# Revit family: TD92_BPA386_AMA003_RVT20_R00
name_source: partatom
category: Mobiliário
units: mm (PartAtom-declared; Revit-internal decimal feet)

## family parameters
Com base no plano de trabalho = Não
Compartilhado = Não
Corte com vazios quando carregada = Não
Número OmniClass = 23.40.20.00
Ponto de cálculo do ambiente = Não
Sempre na vertical = Sim
Título OmniClass = General Furniture and Specialties

## types (1)
- TD92_BPA386_AMA003_RVT20_R00
    Descrição = Para deixar os pequenos mais confortáveis, o Banco Infantil Tramontina Pause em Polietileno é a escolha ideal! Ele é composto por quatro peças coloridas de fácil encaixe e fica perfeito em playgrounds residenciais ou comerciais. Indicado para crianças na faixa etária dos 3 anos de idade e para até 80 kg de alegria e diversão, ele vai compor os ambientes das crianças com muito mais cor e felicidade!
    Elevação padrão = 0  [stored 0 ft]
    Fabricante = Tramontina Delta S/A
    Modelo = Banco Infantil Tramontina Pause em Polietileno Amarelo
    Nota-chave = 92386003
    URL = https://www.tramontinastore.com

note: [stored X ft] marks values corroborated as IEEE doubles in the binary element streams (Revit-internal decimal feet)
